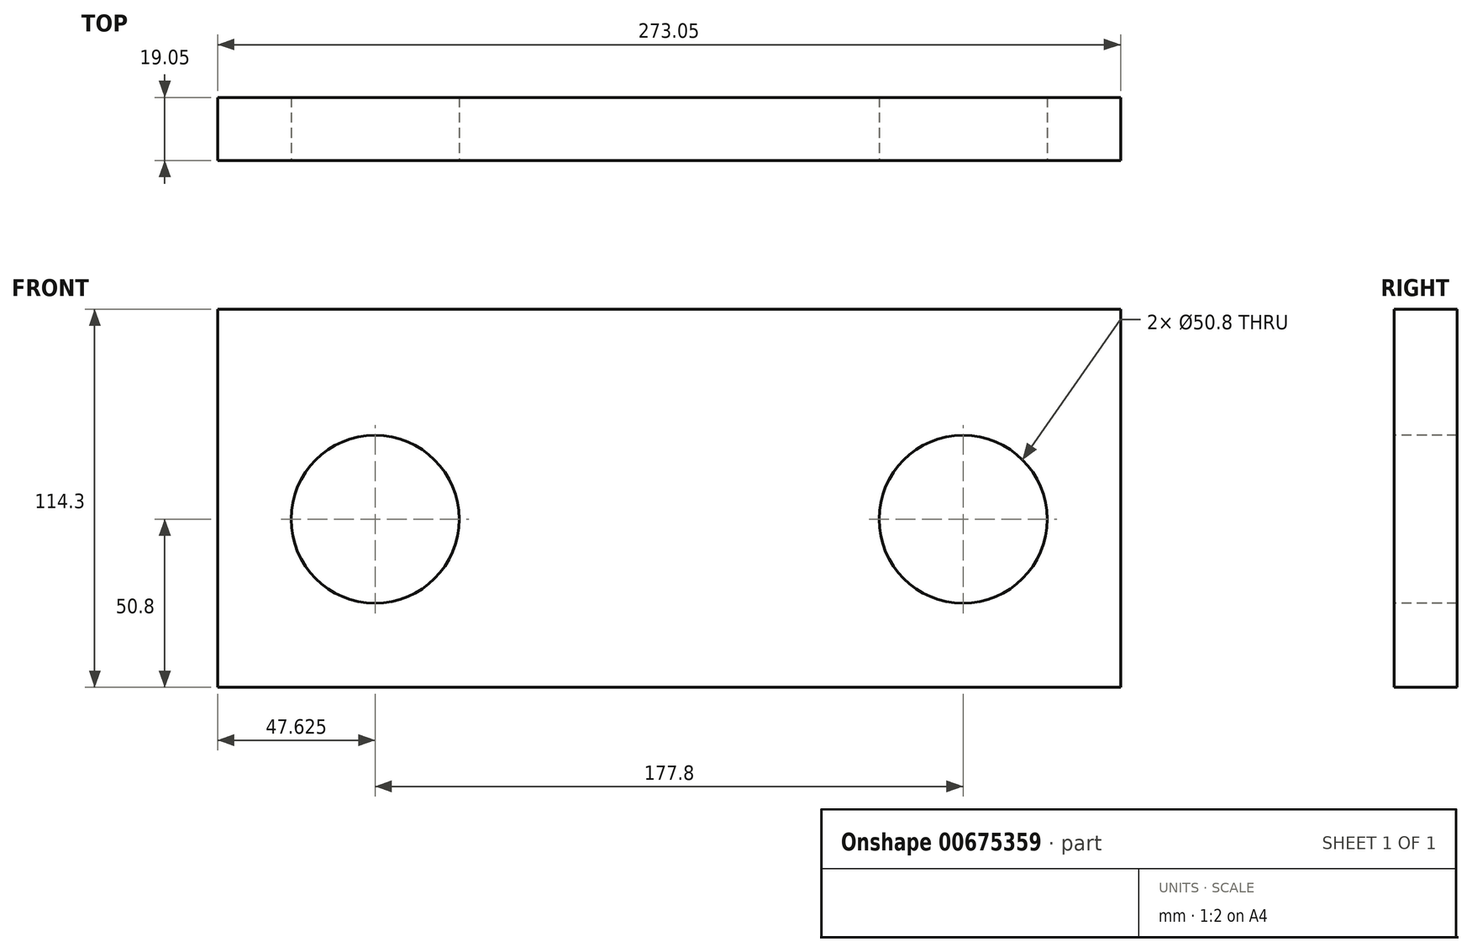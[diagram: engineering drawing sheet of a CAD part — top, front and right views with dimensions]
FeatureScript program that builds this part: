
annotation { "Feature Type Name" : "Feature", "Feature Type Description" : "" }
export const myFeature = defineFeature(function(context is Context, id is Id, definition is map)
    precondition{}
    {
        {
            var Q0;
            Q0=qCreatedBy(makeId("Front.planeOp"),FACE);
            var sketch = newSketch(context, id + "F0", { "sketchPlane" : qUnion([Q0])});
            skLineSegment(sketch, "E0.bottom", {"start": v(0, 0) * mm, "end": v(273.05, 0) * mm});
            skLineSegment(sketch, "E0.top", {"start": v(0, 114.3) * mm, "end": v(273.05, 114.3) * mm});
            skLineSegment(sketch, "E0.left", {"start": v(0, 0) * mm, "end": v(0, 114.3) * mm});
            skLineSegment(sketch, "E0.right", {"start": v(273.05, 0) * mm, "end": v(273.05, 114.3) * mm});
            skSolve(sketch);
        }
        {
            var Q0;
            Q0 = qSketchRegion(id + "F0", true);
            extrude(context, id + "F1", {"entities" : qUnion([Q0]), "depth" : 19.05 * mm, "offsetDistance" : 25.4 * mm});
        }
        {
            var Q0;
            Q0=makeQuery(id+"F1.opExtrude","CAP_FACE",FACE,{"disambiguationData":[OSD([sQuery(id+"F0.wireOp",EDGE,"E0.bottom"),sQuery(id+"F0.wireOp",EDGE,"E0.top"),sQuery(id+"F0.wireOp",EDGE,"E0.left"),sQuery(id+"F0.wireOp",EDGE,"E0.right")])],"isStart":false});
            var sketch = newSketch(context, id + "F2", { "sketchPlane" : qUnion([Q0])});
            skCircle(sketch, "E1", {"center": v(47.63, 50.8) * mm, "radius": 25.4 * mm});
            skSolve(sketch);
        }
        {
            var Q0;
            Q0=makeQuery(id+"F2.imprint","IMPRINT",FACE,{"disambiguationData":[TD([[makeQuery(id+"F2.imprint","IMPRINT",EDGE,{"derivedFrom":sQuery(id+"F2.wireOp",EDGE,"E1")}),-1.0]])]});
            var sketch = newSketch(context, id + "F3", { "sketchPlane" : qUnion([Q0])});
            skCircle(sketch, "E2", {"center": v(225.43, 50.8) * mm, "radius": 25.4 * mm});
            skSolve(sketch);
        }
        {
            var Q0;
            Q0=makeQuery(id+"F2.imprint","IMPRINT",FACE,{"disambiguationData":[TD([[makeQuery(id+"F2.imprint","IMPRINT",EDGE,{"derivedFrom":sQuery(id+"F2.wireOp",EDGE,"E1")}),1.0]])]});
            extrude(context, id + "F4", {"entities" : qUnion([Q0]), "operationType" : NewBodyOperationType.REMOVE, "oppositeDirection" : true, "depth" : 25.4 * mm, "offsetDistance" : 25.4 * mm});
        }
        {
            var Q0;
            Q0=makeQuery(id+"F3.imprint","IMPRINT",FACE,{"disambiguationData":[TD([[makeQuery(id+"F3.imprint","IMPRINT",EDGE,{"derivedFrom":sQuery(id+"F3.wireOp",EDGE,"E2")}),1.0]])]});
            extrude(context, id + "F5", {"entities" : qUnion([Q0]), "operationType" : NewBodyOperationType.REMOVE, "oppositeDirection" : true, "depth" : 25.4 * mm, "offsetDistance" : 25.4 * mm});
        }
    });
